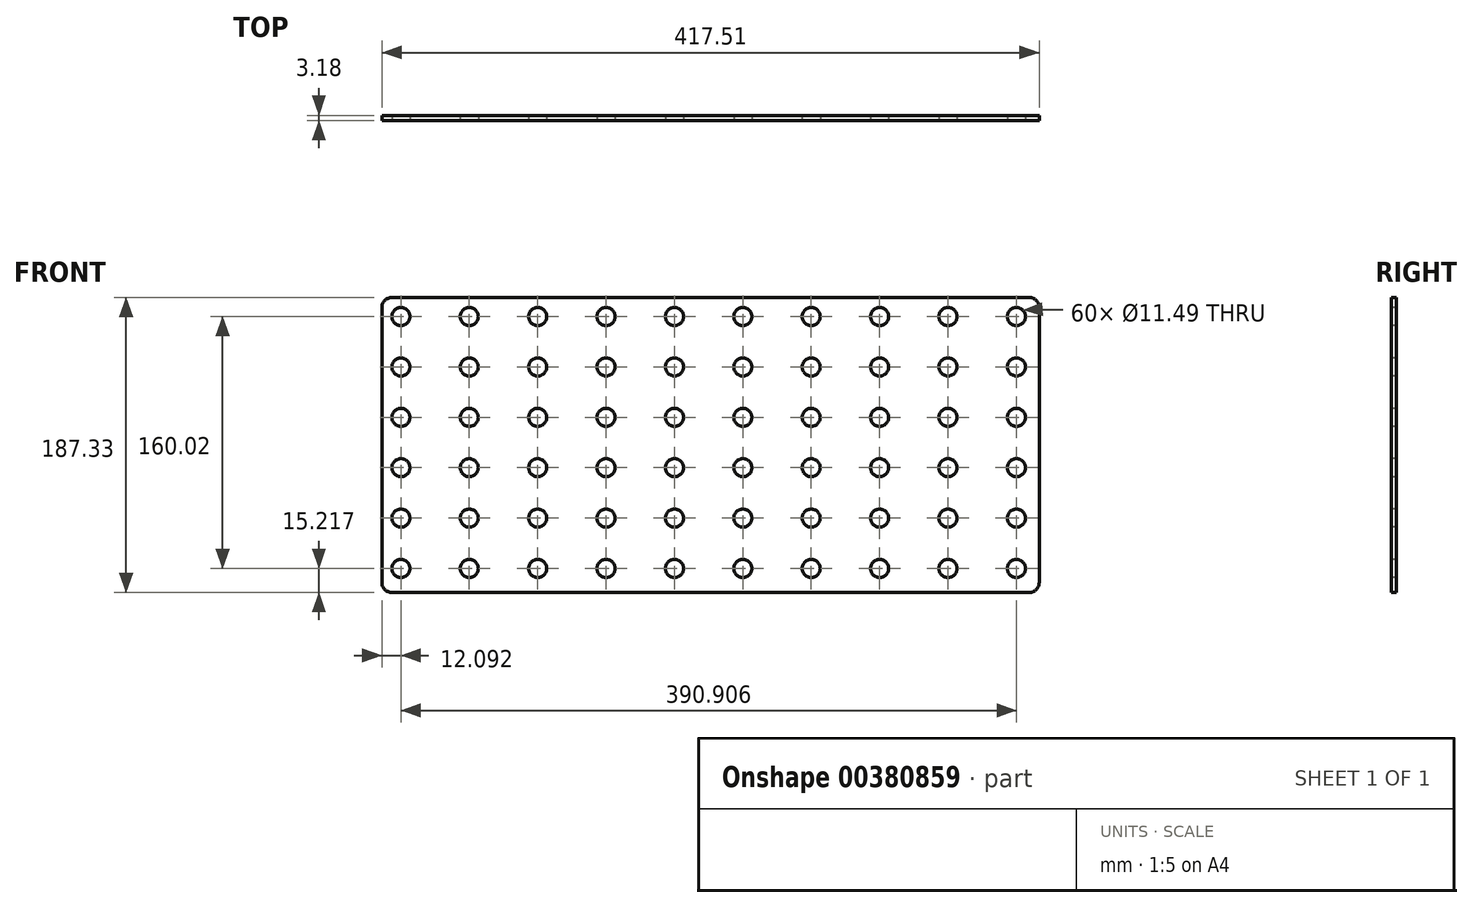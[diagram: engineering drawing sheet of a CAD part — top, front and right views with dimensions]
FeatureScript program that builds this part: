
annotation { "Feature Type Name" : "Feature", "Feature Type Description" : "" }
export const myFeature = defineFeature(function(context is Context, id is Id, definition is map)
    precondition{}
    {
        {
            var Q0;
            Q0=qCreatedBy(makeId("Front.planeOp"),FACE);
            var sketch = newSketch(context, id + "F0", { "sketchPlane" : qUnion([Q0])});
            skLineSegment(sketch, "E0.bottom", {"start": v(-85.54, 88.82) * mm, "end": v(319.27, 88.82) * mm});
            skLineSegment(sketch, "E0.top", {"start": v(-85.54, -98.5) * mm, "end": v(319.27, -98.5) * mm});
            skLineSegment(sketch, "E0.left", {"start": v(-91.9, 82.47) * mm, "end": v(-91.9, -92.16) * mm});
            skLineSegment(sketch, "E0.right", {"start": v(325.62, 82.47) * mm, "end": v(325.62, -92.16) * mm});
            skCircle(sketch, "E1", {"center": v(-79.8, 76.73) * mm, "radius": 5.74 * mm});
            skCircle(sketch, "E2.0.1.0", {"center": v(-79.8, 44.72) * mm, "radius": 5.74 * mm});
            skCircle(sketch, "E2.0.2.0", {"center": v(-79.8, 12.72) * mm, "radius": 5.74 * mm});
            skCircle(sketch, "E2.0.3.0", {"center": v(-79.8, -19.28) * mm, "radius": 5.74 * mm});
            skCircle(sketch, "E2.0.4.0", {"center": v(-79.8, -51.29) * mm, "radius": 5.74 * mm});
            skCircle(sketch, "E2.0.5.0", {"center": v(-79.8, -83.3) * mm, "radius": 5.74 * mm});
            skCircle(sketch, "E2.1.0.0", {"center": v(-36.36, 76.73) * mm, "radius": 5.74 * mm});
            skCircle(sketch, "E2.1.1.0", {"center": v(-36.36, 44.72) * mm, "radius": 5.74 * mm});
            skCircle(sketch, "E2.1.2.0", {"center": v(-36.36, 12.72) * mm, "radius": 5.74 * mm});
            skCircle(sketch, "E2.1.3.0", {"center": v(-36.36, -19.28) * mm, "radius": 5.74 * mm});
            skCircle(sketch, "E2.1.4.0", {"center": v(-36.36, -51.29) * mm, "radius": 5.74 * mm});
            skCircle(sketch, "E2.1.5.0", {"center": v(-36.36, -83.3) * mm, "radius": 5.74 * mm});
            skCircle(sketch, "E2.2.0.0", {"center": v(7.07, 76.73) * mm, "radius": 5.74 * mm});
            skCircle(sketch, "E2.2.1.0", {"center": v(7.07, 44.72) * mm, "radius": 5.74 * mm});
            skCircle(sketch, "E2.2.2.0", {"center": v(7.07, 12.72) * mm, "radius": 5.74 * mm});
            skCircle(sketch, "E2.2.3.0", {"center": v(7.07, -19.28) * mm, "radius": 5.74 * mm});
            skCircle(sketch, "E2.2.4.0", {"center": v(7.07, -51.29) * mm, "radius": 5.74 * mm});
            skCircle(sketch, "E2.2.5.0", {"center": v(7.07, -83.3) * mm, "radius": 5.74 * mm});
            skCircle(sketch, "E2.3.0.0", {"center": v(50.5, 76.73) * mm, "radius": 5.74 * mm});
            skCircle(sketch, "E2.3.1.0", {"center": v(50.5, 44.72) * mm, "radius": 5.74 * mm});
            skCircle(sketch, "E2.3.2.0", {"center": v(50.5, 12.72) * mm, "radius": 5.74 * mm});
            skCircle(sketch, "E2.3.3.0", {"center": v(50.5, -19.28) * mm, "radius": 5.74 * mm});
            skCircle(sketch, "E2.3.4.0", {"center": v(50.5, -51.29) * mm, "radius": 5.74 * mm});
            skCircle(sketch, "E2.3.5.0", {"center": v(50.5, -83.3) * mm, "radius": 5.74 * mm});
            skCircle(sketch, "E2.4.0.0", {"center": v(93.94, 76.73) * mm, "radius": 5.74 * mm});
            skCircle(sketch, "E2.4.1.0", {"center": v(93.94, 44.72) * mm, "radius": 5.74 * mm});
            skCircle(sketch, "E2.4.2.0", {"center": v(93.94, 12.72) * mm, "radius": 5.74 * mm});
            skCircle(sketch, "E2.4.3.0", {"center": v(93.94, -19.28) * mm, "radius": 5.74 * mm});
            skCircle(sketch, "E2.4.4.0", {"center": v(93.94, -51.29) * mm, "radius": 5.74 * mm});
            skCircle(sketch, "E2.4.5.0", {"center": v(93.94, -83.3) * mm, "radius": 5.74 * mm});
            skCircle(sketch, "E2.5.0.0", {"center": v(137.37, 76.73) * mm, "radius": 5.74 * mm});
            skCircle(sketch, "E2.5.1.0", {"center": v(137.37, 44.72) * mm, "radius": 5.74 * mm});
            skCircle(sketch, "E2.5.2.0", {"center": v(137.37, 12.72) * mm, "radius": 5.74 * mm});
            skCircle(sketch, "E2.5.3.0", {"center": v(137.37, -19.28) * mm, "radius": 5.74 * mm});
            skCircle(sketch, "E2.5.4.0", {"center": v(137.37, -51.29) * mm, "radius": 5.74 * mm});
            skCircle(sketch, "E2.5.5.0", {"center": v(137.37, -83.3) * mm, "radius": 5.74 * mm});
            skCircle(sketch, "E2.6.0.0", {"center": v(180.8, 76.73) * mm, "radius": 5.74 * mm});
            skCircle(sketch, "E2.6.1.0", {"center": v(180.8, 44.72) * mm, "radius": 5.74 * mm});
            skCircle(sketch, "E2.6.2.0", {"center": v(180.8, 12.72) * mm, "radius": 5.74 * mm});
            skCircle(sketch, "E2.6.3.0", {"center": v(180.8, -19.28) * mm, "radius": 5.74 * mm});
            skCircle(sketch, "E2.6.4.0", {"center": v(180.8, -51.29) * mm, "radius": 5.74 * mm});
            skCircle(sketch, "E2.6.5.0", {"center": v(180.8, -83.3) * mm, "radius": 5.74 * mm});
            skCircle(sketch, "E2.7.0.0", {"center": v(224.24, 76.73) * mm, "radius": 5.74 * mm});
            skCircle(sketch, "E2.7.1.0", {"center": v(224.24, 44.72) * mm, "radius": 5.74 * mm});
            skCircle(sketch, "E2.7.2.0", {"center": v(224.24, 12.72) * mm, "radius": 5.74 * mm});
            skCircle(sketch, "E2.7.3.0", {"center": v(224.24, -19.28) * mm, "radius": 5.74 * mm});
            skCircle(sketch, "E2.7.4.0", {"center": v(224.24, -51.29) * mm, "radius": 5.74 * mm});
            skCircle(sketch, "E2.7.5.0", {"center": v(224.24, -83.3) * mm, "radius": 5.74 * mm});
            skCircle(sketch, "E2.8.0.0", {"center": v(267.67, 76.73) * mm, "radius": 5.74 * mm});
            skCircle(sketch, "E2.8.1.0", {"center": v(267.67, 44.72) * mm, "radius": 5.74 * mm});
            skCircle(sketch, "E2.8.2.0", {"center": v(267.67, 12.72) * mm, "radius": 5.74 * mm});
            skCircle(sketch, "E2.8.3.0", {"center": v(267.67, -19.28) * mm, "radius": 5.74 * mm});
            skCircle(sketch, "E2.8.4.0", {"center": v(267.67, -51.29) * mm, "radius": 5.74 * mm});
            skCircle(sketch, "E2.8.5.0", {"center": v(267.67, -83.3) * mm, "radius": 5.74 * mm});
            skCircle(sketch, "E2.9.0.0", {"center": v(311.1, 76.73) * mm, "radius": 5.74 * mm});
            skCircle(sketch, "E2.9.1.0", {"center": v(311.1, 44.72) * mm, "radius": 5.74 * mm});
            skCircle(sketch, "E2.9.2.0", {"center": v(311.1, 12.72) * mm, "radius": 5.74 * mm});
            skCircle(sketch, "E2.9.3.0", {"center": v(311.1, -19.28) * mm, "radius": 5.74 * mm});
            skCircle(sketch, "E2.9.4.0", {"center": v(311.1, -51.29) * mm, "radius": 5.74 * mm});
            skCircle(sketch, "E2.9.5.0", {"center": v(311.1, -83.3) * mm, "radius": 5.74 * mm});
            skLineSegment(sketch, "E2.direction1", {"start": v(-79.8, 76.73) * mm, "end": v(-36.36, 76.73) * mm, "construction": true});
            skLineSegment(sketch, "E2.direction2", {"start": v(-79.8, 76.73) * mm, "end": v(-79.8, 44.72) * mm, "construction": true});
            skPoint(sketch, "E3.visualSharp", {"position": v(-91.9, 88.82) * mm});
            skArc(sketch, "E3.filletArc", {"start": v(-85.54, 88.82) * mm, "mid": v(-90.03, 86.96) * mm, "end": v(-91.9, 82.47) * mm});
            skPoint(sketch, "E4.visualSharp", {"position": v(325.62, 88.82) * mm});
            skArc(sketch, "E4.filletArc", {"start": v(325.62, 82.47) * mm, "mid": v(323.76, 86.96) * mm, "end": v(319.27, 88.82) * mm});
            skPoint(sketch, "E5.visualSharp", {"position": v(325.62, -98.5) * mm});
            skArc(sketch, "E5.filletArc", {"start": v(319.27, -98.5) * mm, "mid": v(323.76, -96.65) * mm, "end": v(325.62, -92.16) * mm});
            skPoint(sketch, "E6.visualSharp", {"position": v(-91.9, -98.5) * mm});
            skArc(sketch, "E6.filletArc", {"start": v(-91.9, -92.16) * mm, "mid": v(-90.03, -96.65) * mm, "end": v(-85.54, -98.5) * mm});
            skSolve(sketch);
        }
        {
            var Q0;
            Q0=makeQuery(id+"F0.imprint","IMPRINT",FACE,{"disambiguationData":[TD([[makeQuery(id+"F0.imprint","IMPRINT",EDGE,{"derivedFrom":sQuery(id+"F0.wireOp",EDGE,"E0.bottom")}),-1.0]])]});
            extrude(context, id + "F1", {"entities" : qUnion([Q0]), "oppositeDirection" : true, "depth" : 3.17 * mm});
        }
    });
